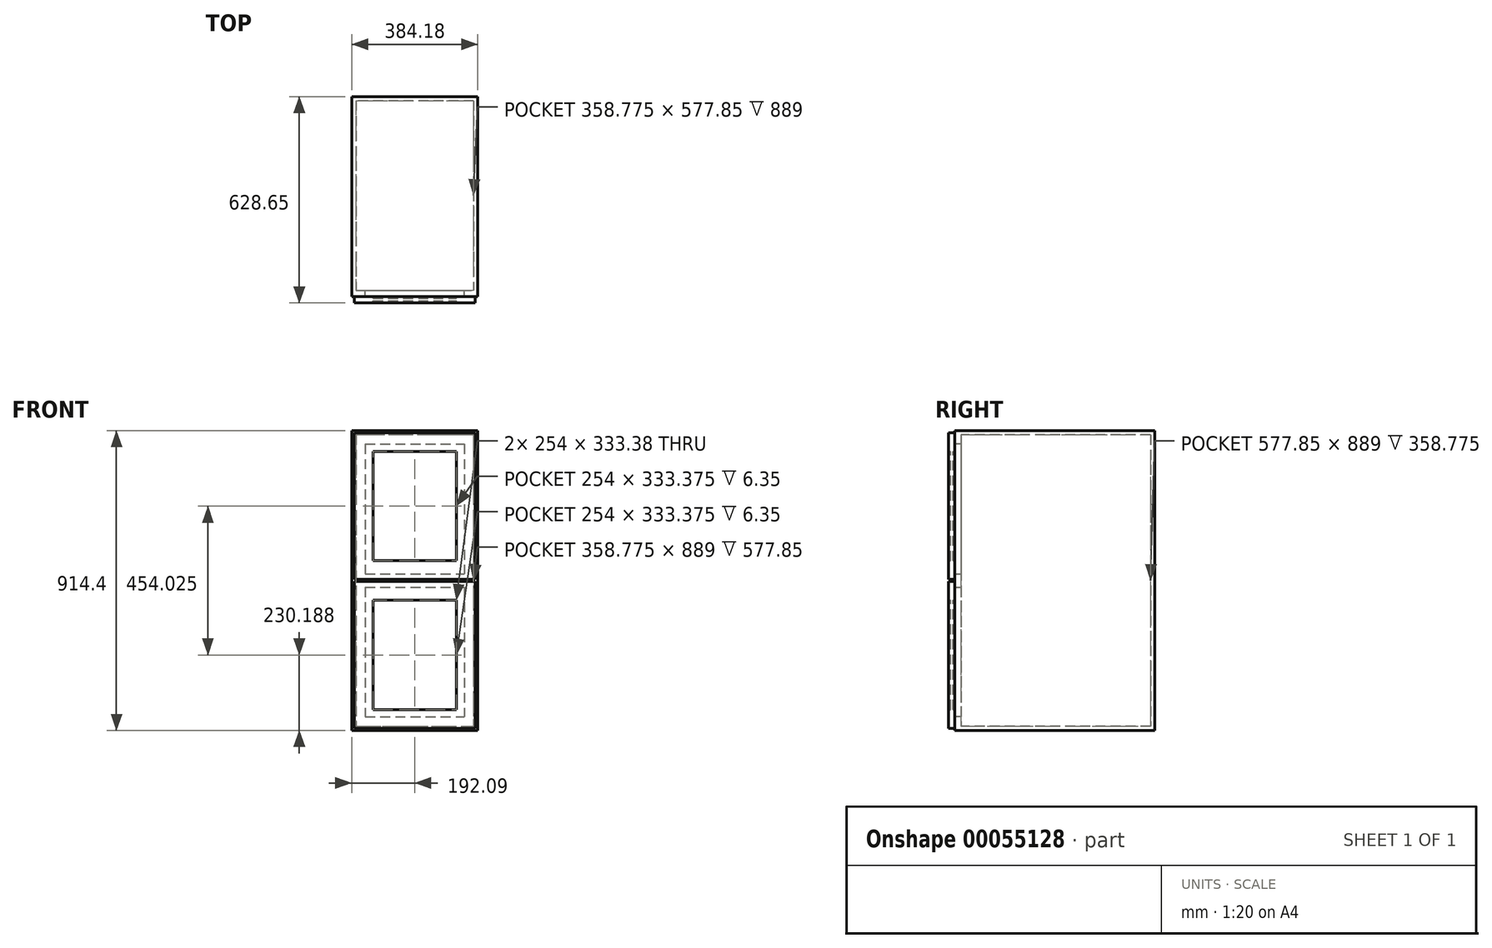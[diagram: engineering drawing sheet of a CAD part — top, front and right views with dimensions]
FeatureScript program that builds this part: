
annotation { "Feature Type Name" : "Feature", "Feature Type Description" : "" }
export const myFeature = defineFeature(function(context is Context, id is Id, definition is map)
    precondition{}
    {
        {
            var Q0;
            Q0=qCreatedBy(makeId("Top.planeOp"),FACE);
            var sketch = newSketch(context, id + "F0", { "sketchPlane" : qUnion([Q0])});
            skLineSegment(sketch, "E0.rect.bottom", {"start": v(192.09, 304.8) * mm, "end": v(-192.09, 304.8) * mm});
            skLineSegment(sketch, "E0.rect.top", {"start": v(192.09, -304.8) * mm, "end": v(-192.09, -304.8) * mm});
            skLineSegment(sketch, "E0.rect.left", {"start": v(192.09, 304.8) * mm, "end": v(192.09, -304.8) * mm});
            skLineSegment(sketch, "E0.rect.right", {"start": v(-192.09, 304.8) * mm, "end": v(-192.09, -304.8) * mm});
            skPoint(sketch, "E0.rect.middle", {"position": v(0, 0) * mm});
            skSolve(sketch);
        }
        {
            var Q0;
            Q0=qSketchRegion(id+"F0",true);
            extrude(context, id + "F1", {"entities" : qUnion([Q0]), "depth" : 914.4 * mm});
        }
        {
            var Q0;
            Q0=makeQuery(id+"F1.opExtrude","SWEPT_FACE",FACE,{"disambiguationData":[OSD([sQuery(id+"F0.wireOp",EDGE,"E0.rect.top")])]});
            shell(context, id + "F2", {"entities" : qUnion([Q0]), "thickness" : 12.7 * mm});
        }
        {
            var Q0;
            Q0=makeQuery(id+"F1.opExtrude","SWEPT_FACE",FACE,{"disambiguationData":[OSD([sQuery(id+"F0.wireOp",EDGE,"E0.rect.top")])]});
            var sketch = newSketch(context, id + "F3", { "sketchPlane" : qUnion([Q0])});
            skLineSegment(sketch, "E1", {"start": v(-192.09, 457.2) * mm, "end": v(192.09, 457.2) * mm, "construction": true});
            skLineSegment(sketch, "E2.rect.bottom", {"start": v(-192.09, 436.56) * mm, "end": v(192.09, 436.56) * mm});
            skLineSegment(sketch, "E2.rect.top", {"start": v(-192.09, 477.84) * mm, "end": v(192.09, 477.84) * mm});
            skLineSegment(sketch, "E2.rect.left", {"start": v(-192.09, 436.56) * mm, "end": v(-192.09, 477.84) * mm});
            skLineSegment(sketch, "E2.rect.right", {"start": v(192.09, 436.56) * mm, "end": v(192.09, 477.84) * mm});
            skPoint(sketch, "E2.rect.middle", {"position": v(0, 457.2) * mm});
            skLineSegment(sketch, "E3.bottom", {"start": v(-184.15, 6.35) * mm, "end": v(184.15, 6.35) * mm});
            skLineSegment(sketch, "E3.top", {"start": v(-184.15, 454.03) * mm, "end": v(184.15, 454.03) * mm});
            skLineSegment(sketch, "E3.left", {"start": v(-184.15, 6.35) * mm, "end": v(-184.15, 454.03) * mm});
            skLineSegment(sketch, "E3.right", {"start": v(184.15, 6.35) * mm, "end": v(184.15, 454.03) * mm});
            skLineSegment(sketch, "E4.rect.bottom", {"start": v(-150.81, 873.13) * mm, "end": v(150.81, 873.13) * mm});
            skLineSegment(sketch, "E4.rect.top", {"start": v(-150.81, 41.28) * mm, "end": v(150.81, 41.28) * mm});
            skLineSegment(sketch, "E4.rect.left", {"start": v(-150.81, 873.13) * mm, "end": v(-150.81, 41.28) * mm});
            skLineSegment(sketch, "E4.rect.right", {"start": v(150.81, 873.13) * mm, "end": v(150.81, 41.28) * mm});
            skLineSegment(sketch, "E5.bottom", {"start": v(-127, 63.5) * mm, "end": v(127, 63.5) * mm});
            skLineSegment(sketch, "E5.top", {"start": v(-127, 396.88) * mm, "end": v(127, 396.88) * mm});
            skLineSegment(sketch, "E5.left", {"start": v(-127, 63.5) * mm, "end": v(-127, 396.88) * mm});
            skLineSegment(sketch, "E5.right", {"start": v(127, 63.5) * mm, "end": v(127, 396.88) * mm});
            skLineSegment(sketch, "E6.bottom", {"start": v(-184.15, 460.38) * mm, "end": v(184.15, 460.38) * mm});
            skLineSegment(sketch, "E6.top", {"start": v(-184.15, 908.05) * mm, "end": v(184.15, 908.05) * mm});
            skLineSegment(sketch, "E6.left", {"start": v(-184.15, 460.38) * mm, "end": v(-184.15, 908.05) * mm});
            skLineSegment(sketch, "E6.right", {"start": v(184.15, 460.38) * mm, "end": v(184.15, 908.05) * mm});
            skLineSegment(sketch, "E7.bottom", {"start": v(-127, 517.53) * mm, "end": v(127, 517.53) * mm});
            skLineSegment(sketch, "E7.top", {"start": v(-127, 850.9) * mm, "end": v(127, 850.9) * mm});
            skLineSegment(sketch, "E7.left", {"start": v(-127, 517.53) * mm, "end": v(-127, 850.9) * mm});
            skLineSegment(sketch, "E7.right", {"start": v(127, 517.53) * mm, "end": v(127, 850.9) * mm});
            skSolve(sketch);
        }
        {
            var Q0;
            {var subQ9=sQuery(id+"F3.wireOp",EDGE,"E2.rect.left");Q0=makeQuery(id+"F3.imprint","IMPRINT",FACE,{"disambiguationData":[TD([[makeQuery(id+"F3.imprint","IMPRINT",EDGE,{"derivedFrom":subQ9}),1.0]])]});}
            var Q1;
            {var subQ0=sQuery(id+"F3.wireOp",EDGE,"E4.rect.left");var subQ1=sQuery(id+"F3.wireOp",EDGE,"E2.rect.bottom");var subQ2=makeQuery(id+"F3.imprint","INTERSECT",VERTEX,{"derivedFrom":[subQ1,subQ0]});Q1=makeQuery(id+"F3.imprint","IMPRINT",FACE,{"disambiguationData":[TD([[makeQuery(id+"F3.imprint","IMPRINT",EDGE,{"disambiguationData":[TD([[subQ2,1.0]])],"derivedFrom":subQ0}),-1.0]])]});}
            var Q2;
            {var subQ0=sQuery(id+"F3.wireOp",EDGE,"E4.rect.left");var subQ1=sQuery(id+"F3.wireOp",EDGE,"E2.rect.top");var subQ2=makeQuery(id+"F3.imprint","INTERSECT",VERTEX,{"derivedFrom":[subQ1,subQ0]});Q2=makeQuery(id+"F3.imprint","IMPRINT",FACE,{"disambiguationData":[TD([[makeQuery(id+"F3.imprint","IMPRINT",EDGE,{"disambiguationData":[TD([[subQ2,-1.0]])],"derivedFrom":subQ0}),-1.0]])]});}
            var Q3;
            {var subQ0=sQuery(id+"F3.wireOp",EDGE,"E4.rect.left");var subQ1=sQuery(id+"F3.wireOp",EDGE,"E2.rect.bottom");var subQ2=makeQuery(id+"F3.imprint","INTERSECT",VERTEX,{"derivedFrom":[subQ1,subQ0]});Q3=makeQuery(id+"F3.imprint","IMPRINT",FACE,{"disambiguationData":[TD([[makeQuery(id+"F3.imprint","IMPRINT",EDGE,{"disambiguationData":[TD([[subQ2,-1.0]])],"derivedFrom":subQ1}),1.0]])]});}
            var Q4;
            {var subQ0=sQuery(id+"F3.wireOp",EDGE,"E4.rect.left");var subQ1=sQuery(id+"F3.wireOp",EDGE,"E2.rect.top");var subQ2=makeQuery(id+"F3.imprint","INTERSECT",VERTEX,{"derivedFrom":[subQ1,subQ0]});Q4=makeQuery(id+"F3.imprint","IMPRINT",FACE,{"disambiguationData":[TD([[makeQuery(id+"F3.imprint","IMPRINT",EDGE,{"disambiguationData":[TD([[subQ2,-1.0]])],"derivedFrom":subQ1}),-1.0]])]});}
            var Q5;
            {var subQ0=sQuery(id+"F3.wireOp",EDGE,"E4.rect.right");var subQ1=sQuery(id+"F3.wireOp",EDGE,"E2.rect.bottom");var subQ2=makeQuery(id+"F3.imprint","INTERSECT",VERTEX,{"derivedFrom":[subQ1,subQ0]});Q5=makeQuery(id+"F3.imprint","IMPRINT",FACE,{"disambiguationData":[TD([[makeQuery(id+"F3.imprint","IMPRINT",EDGE,{"disambiguationData":[TD([[subQ2,1.0]])],"derivedFrom":subQ0}),1.0]])]});}
            var Q6;
            {var subQ0=sQuery(id+"F3.wireOp",EDGE,"E4.rect.right");var subQ1=sQuery(id+"F3.wireOp",EDGE,"E2.rect.top");var subQ2=makeQuery(id+"F3.imprint","INTERSECT",VERTEX,{"derivedFrom":[subQ1,subQ0]});Q6=makeQuery(id+"F3.imprint","IMPRINT",FACE,{"disambiguationData":[TD([[makeQuery(id+"F3.imprint","IMPRINT",EDGE,{"disambiguationData":[TD([[subQ2,-1.0]])],"derivedFrom":subQ0}),1.0]])]});}
            var Q7;
            {var subQ0=sQuery(id+"F3.wireOp",EDGE,"E2.rect.right");Q7=makeQuery(id+"F3.imprint","IMPRINT",FACE,{"disambiguationData":[TD([[makeQuery(id+"F3.imprint","IMPRINT",EDGE,{"derivedFrom":subQ0}),-1.0]])]});}
            var Q8;
            {var subQ0=sQuery(id+"F3.wireOp",EDGE,"E3.right");var subQ5=sQuery(id+"F3.wireOp",EDGE,"E3.top");var subQ6=makeQuery(id+"F3.imprint","INTERSECT",VERTEX,{"derivedFrom":[subQ5,subQ0]});Q8=makeQuery(id+"F3.imprint","IMPRINT",FACE,{"disambiguationData":[TD([[makeQuery(id+"F3.imprint","IMPRINT",EDGE,{"disambiguationData":[TD([[subQ6,1.0]])],"derivedFrom":subQ0}),1.0]])]});}
            var Q9;
            {var subQ0=sQuery(id+"F3.wireOp",EDGE,"E6.right");var subQ5=sQuery(id+"F3.wireOp",EDGE,"E6.bottom");var subQ6=makeQuery(id+"F3.imprint","INTERSECT",VERTEX,{"derivedFrom":[subQ5,subQ0]});Q9=makeQuery(id+"F3.imprint","IMPRINT",FACE,{"disambiguationData":[TD([[makeQuery(id+"F3.imprint","IMPRINT",EDGE,{"disambiguationData":[TD([[subQ6,-1.0]])],"derivedFrom":subQ0}),1.0]])]});}
            var Q10;
            {var subQ0=sQuery(id+"F3.wireOp",EDGE,"E4.rect.right");var subQ1=sQuery(id+"F3.wireOp",EDGE,"E3.top");var subQ2=makeQuery(id+"F3.imprint","INTERSECT",VERTEX,{"derivedFrom":[subQ1,subQ0]});Q10=makeQuery(id+"F3.imprint","IMPRINT",FACE,{"disambiguationData":[TD([[makeQuery(id+"F3.imprint","IMPRINT",EDGE,{"disambiguationData":[TD([[subQ2,1.0]])],"derivedFrom":subQ0}),1.0]])]});}
            var Q11;
            {var subQ0=sQuery(id+"F3.wireOp",EDGE,"E4.rect.left");var subQ1=sQuery(id+"F3.wireOp",EDGE,"E3.top");var subQ2=makeQuery(id+"F3.imprint","INTERSECT",VERTEX,{"derivedFrom":[subQ1,subQ0]});Q11=makeQuery(id+"F3.imprint","IMPRINT",FACE,{"disambiguationData":[TD([[makeQuery(id+"F3.imprint","IMPRINT",EDGE,{"disambiguationData":[TD([[subQ2,1.0]])],"derivedFrom":subQ0}),-1.0]])]});}
            var Q12;
            {var subQ0=sQuery(id+"F3.wireOp",EDGE,"E3.left");var subQ5=sQuery(id+"F3.wireOp",EDGE,"E3.top");var subQ6=makeQuery(id+"F3.imprint","INTERSECT",VERTEX,{"derivedFrom":[subQ5,subQ0]});Q12=makeQuery(id+"F3.imprint","IMPRINT",FACE,{"disambiguationData":[TD([[makeQuery(id+"F3.imprint","IMPRINT",EDGE,{"disambiguationData":[TD([[subQ6,1.0]])],"derivedFrom":subQ0}),-1.0]])]});}
            var Q13;
            {var subQ0=sQuery(id+"F3.wireOp",EDGE,"E6.left");var subQ5=sQuery(id+"F3.wireOp",EDGE,"E6.bottom");var subQ6=makeQuery(id+"F3.imprint","INTERSECT",VERTEX,{"derivedFrom":[subQ5,subQ0]});Q13=makeQuery(id+"F3.imprint","IMPRINT",FACE,{"disambiguationData":[TD([[makeQuery(id+"F3.imprint","IMPRINT",EDGE,{"disambiguationData":[TD([[subQ6,-1.0]])],"derivedFrom":subQ0}),-1.0]])]});}
            var Q14;
            {var subQ0=sQuery(id+"F3.wireOp",EDGE,"E4.rect.left");var subQ1=sQuery(id+"F3.wireOp",EDGE,"E3.top");var subQ2=makeQuery(id+"F3.imprint","INTERSECT",VERTEX,{"derivedFrom":[subQ1,subQ0]});Q14=makeQuery(id+"F3.imprint","IMPRINT",FACE,{"disambiguationData":[TD([[makeQuery(id+"F3.imprint","IMPRINT",EDGE,{"disambiguationData":[TD([[subQ2,-1.0]])],"derivedFrom":subQ1}),1.0]])]});}
            extrude(context, id + "F4", {"entities" : qUnion([Q0, Q1, Q2, Q3, Q4, Q5, Q6, Q7, Q8, Q9, Q10, Q11, Q12, Q13, Q14]), "operationType" : NewBodyOperationType.ADD, "oppositeDirection" : true, "depth" : 19.05 * mm});
        }
        {
            var Q0;
            {var subQ1=sQuery(id+"F3.wireOp",EDGE,"E4.rect.bottom");Q0=makeQuery(id+"F3.imprint","IMPRINT",FACE,{"disambiguationData":[TD([[makeQuery(id+"F3.imprint","IMPRINT",EDGE,{"derivedFrom":subQ1}),1.0]])]});}
            var Q1;
            {var subQ0=sQuery(id+"F0.wireOp",EDGE,"E0.rect.top");var subQ1=makeQuery(id+"F1.opExtrude","CAP_EDGE",EDGE,{"disambiguationData":[OSD([subQ0])],"isStart":false});Q1=makeQuery(id+"F3.imprint","IMPRINT",FACE,{"disambiguationData":[TD([[makeQuery(id+"F3.imprint","IMPRINT",EDGE,{"derivedFrom":subQ1}),1.0]])]});}
            var Q2;
            {var subQ0=sQuery(id+"F3.wireOp",EDGE,"E4.rect.top");Q2=makeQuery(id+"F3.imprint","IMPRINT",FACE,{"disambiguationData":[TD([[makeQuery(id+"F3.imprint","IMPRINT",EDGE,{"derivedFrom":subQ0}),-1.0]])]});}
            var Q3;
            {var subQ1=sQuery(id+"F3.wireOp",EDGE,"E3.bottom");Q3=makeQuery(id+"F3.imprint","IMPRINT",FACE,{"disambiguationData":[TD([[makeQuery(id+"F3.imprint","IMPRINT",EDGE,{"derivedFrom":subQ1}),-1.0]])]});}
            var Q4;
            {var subQ0=sQuery(id+"F3.wireOp",EDGE,"E3.bottom");Q4=makeQuery(id+"F3.imprint","IMPRINT",FACE,{"disambiguationData":[TD([[makeQuery(id+"F3.imprint","IMPRINT",EDGE,{"derivedFrom":subQ0}),1.0]])]});}
            var Q5;
            {var subQ0=sQuery(id+"F3.wireOp",EDGE,"E4.rect.left");var subQ1=sQuery(id+"F3.wireOp",EDGE,"E2.rect.bottom");var subQ2=makeQuery(id+"F3.imprint","INTERSECT",VERTEX,{"derivedFrom":[subQ1,subQ0]});Q5=makeQuery(id+"F3.imprint","IMPRINT",FACE,{"disambiguationData":[TD([[makeQuery(id+"F3.imprint","IMPRINT",EDGE,{"disambiguationData":[TD([[subQ2,1.0]])],"derivedFrom":subQ0}),-1.0]])]});}
            var Q6;
            {var subQ0=sQuery(id+"F3.wireOp",EDGE,"E2.rect.left");Q6=makeQuery(id+"F3.imprint","IMPRINT",FACE,{"disambiguationData":[TD([[makeQuery(id+"F3.imprint","IMPRINT",EDGE,{"derivedFrom":subQ0}),1.0]])]});}
            var Q7;
            {var subQ0=sQuery(id+"F3.wireOp",EDGE,"E3.left");var subQ5=sQuery(id+"F3.wireOp",EDGE,"E3.top");var subQ6=makeQuery(id+"F3.imprint","INTERSECT",VERTEX,{"derivedFrom":[subQ5,subQ0]});Q7=makeQuery(id+"F3.imprint","IMPRINT",FACE,{"disambiguationData":[TD([[makeQuery(id+"F3.imprint","IMPRINT",EDGE,{"disambiguationData":[TD([[subQ6,1.0]])],"derivedFrom":subQ0}),-1.0]])]});}
            var Q8;
            {var subQ0=sQuery(id+"F3.wireOp",EDGE,"E4.rect.left");var subQ1=sQuery(id+"F3.wireOp",EDGE,"E2.rect.top");var subQ2=makeQuery(id+"F3.imprint","INTERSECT",VERTEX,{"derivedFrom":[subQ1,subQ0]});Q8=makeQuery(id+"F3.imprint","IMPRINT",FACE,{"disambiguationData":[TD([[makeQuery(id+"F3.imprint","IMPRINT",EDGE,{"disambiguationData":[TD([[subQ2,-1.0]])],"derivedFrom":subQ0}),-1.0]])]});}
            var Q9;
            {var subQ0=sQuery(id+"F3.wireOp",EDGE,"E4.rect.right");var subQ1=sQuery(id+"F3.wireOp",EDGE,"E2.rect.top");var subQ2=makeQuery(id+"F3.imprint","INTERSECT",VERTEX,{"derivedFrom":[subQ1,subQ0]});Q9=makeQuery(id+"F3.imprint","IMPRINT",FACE,{"disambiguationData":[TD([[makeQuery(id+"F3.imprint","IMPRINT",EDGE,{"disambiguationData":[TD([[subQ2,-1.0]])],"derivedFrom":subQ0}),1.0]])]});}
            var Q10;
            {var subQ0=sQuery(id+"F3.wireOp",EDGE,"E4.rect.right");var subQ1=sQuery(id+"F3.wireOp",EDGE,"E2.rect.bottom");var subQ2=makeQuery(id+"F3.imprint","INTERSECT",VERTEX,{"derivedFrom":[subQ1,subQ0]});Q10=makeQuery(id+"F3.imprint","IMPRINT",FACE,{"disambiguationData":[TD([[makeQuery(id+"F3.imprint","IMPRINT",EDGE,{"disambiguationData":[TD([[subQ2,1.0]])],"derivedFrom":subQ0}),1.0]])]});}
            var Q11;
            {var subQ7=sQuery(id+"F3.wireOp",EDGE,"E2.rect.right");Q11=makeQuery(id+"F3.imprint","IMPRINT",FACE,{"disambiguationData":[TD([[makeQuery(id+"F3.imprint","IMPRINT",EDGE,{"derivedFrom":subQ7}),-1.0]])]});}
            var Q12;
            {var subQ0=sQuery(id+"F3.wireOp",EDGE,"E3.right");var subQ5=sQuery(id+"F3.wireOp",EDGE,"E3.top");var subQ6=makeQuery(id+"F3.imprint","INTERSECT",VERTEX,{"derivedFrom":[subQ5,subQ0]});Q12=makeQuery(id+"F3.imprint","IMPRINT",FACE,{"disambiguationData":[TD([[makeQuery(id+"F3.imprint","IMPRINT",EDGE,{"disambiguationData":[TD([[subQ6,1.0]])],"derivedFrom":subQ0}),1.0]])]});}
            extrude(context, id + "F5", {"entities" : qUnion([Q0, Q1, Q2, Q3, Q4, Q5, Q6, Q7, Q8, Q9, Q10, Q11, Q12]), "operationType" : NewBodyOperationType.ADD, "oppositeDirection" : true, "depth" : 19.05 * mm});
        }
        {
            var Q0;
            {var subQ0=sQuery(id+"F3.wireOp",EDGE,"E4.rect.top");Q0=makeQuery(id+"F3.imprint","IMPRINT",FACE,{"disambiguationData":[TD([[makeQuery(id+"F3.imprint","IMPRINT",EDGE,{"derivedFrom":subQ0}),-1.0]])]});}
            var Q1;
            {var subQ0=sQuery(id+"F3.wireOp",EDGE,"E3.bottom");Q1=makeQuery(id+"F3.imprint","IMPRINT",FACE,{"disambiguationData":[TD([[makeQuery(id+"F3.imprint","IMPRINT",EDGE,{"derivedFrom":subQ0}),1.0]])]});}
            var Q2;
            {var subQ1=sQuery(id+"F3.wireOp",EDGE,"E4.rect.top");Q2=makeQuery(id+"F3.imprint","IMPRINT",FACE,{"disambiguationData":[TD([[makeQuery(id+"F3.imprint","IMPRINT",EDGE,{"derivedFrom":subQ1}),1.0]])]});}
            var Q3;
            {var subQ0=sQuery(id+"F3.wireOp",EDGE,"E4.rect.left");var subQ1=sQuery(id+"F3.wireOp",EDGE,"E2.rect.bottom");var subQ2=makeQuery(id+"F3.imprint","INTERSECT",VERTEX,{"derivedFrom":[subQ1,subQ0]});Q3=makeQuery(id+"F3.imprint","IMPRINT",FACE,{"disambiguationData":[TD([[makeQuery(id+"F3.imprint","IMPRINT",EDGE,{"disambiguationData":[TD([[subQ2,-1.0]])],"derivedFrom":subQ1}),1.0]])]});}
            var Q4;
            {var subQ0=sQuery(id+"F3.wireOp",EDGE,"E4.rect.left");var subQ1=sQuery(id+"F3.wireOp",EDGE,"E2.rect.bottom");var subQ2=makeQuery(id+"F3.imprint","INTERSECT",VERTEX,{"derivedFrom":[subQ1,subQ0]});Q4=makeQuery(id+"F3.imprint","IMPRINT",FACE,{"disambiguationData":[TD([[makeQuery(id+"F3.imprint","IMPRINT",EDGE,{"disambiguationData":[TD([[subQ2,1.0]])],"derivedFrom":subQ0}),-1.0]])]});}
            var Q5;
            {var subQ0=sQuery(id+"F3.wireOp",EDGE,"E4.rect.right");var subQ1=sQuery(id+"F3.wireOp",EDGE,"E2.rect.bottom");var subQ2=makeQuery(id+"F3.imprint","INTERSECT",VERTEX,{"derivedFrom":[subQ1,subQ0]});Q5=makeQuery(id+"F3.imprint","IMPRINT",FACE,{"disambiguationData":[TD([[makeQuery(id+"F3.imprint","IMPRINT",EDGE,{"disambiguationData":[TD([[subQ2,1.0]])],"derivedFrom":subQ0}),1.0]])]});}
            var Q6;
            {var subQ0=sQuery(id+"F3.wireOp",EDGE,"E3.right");var subQ5=sQuery(id+"F3.wireOp",EDGE,"E3.top");var subQ6=makeQuery(id+"F3.imprint","INTERSECT",VERTEX,{"derivedFrom":[subQ5,subQ0]});Q6=makeQuery(id+"F3.imprint","IMPRINT",FACE,{"disambiguationData":[TD([[makeQuery(id+"F3.imprint","IMPRINT",EDGE,{"disambiguationData":[TD([[subQ6,1.0]])],"derivedFrom":subQ0}),1.0]])]});}
            var Q7;
            {var subQ0=sQuery(id+"F3.wireOp",EDGE,"E3.left");var subQ5=sQuery(id+"F3.wireOp",EDGE,"E3.top");var subQ6=makeQuery(id+"F3.imprint","INTERSECT",VERTEX,{"derivedFrom":[subQ5,subQ0]});Q7=makeQuery(id+"F3.imprint","IMPRINT",FACE,{"disambiguationData":[TD([[makeQuery(id+"F3.imprint","IMPRINT",EDGE,{"disambiguationData":[TD([[subQ6,1.0]])],"derivedFrom":subQ0}),-1.0]])]});}
            var Q8;
            {var subQ0=sQuery(id+"F3.wireOp",EDGE,"E4.rect.bottom");Q8=makeQuery(id+"F3.imprint","IMPRINT",FACE,{"disambiguationData":[TD([[makeQuery(id+"F3.imprint","IMPRINT",EDGE,{"derivedFrom":subQ0}),1.0]])]});}
            var Q9;
            {var subQ1=sQuery(id+"F3.wireOp",EDGE,"E4.rect.bottom");Q9=makeQuery(id+"F3.imprint","IMPRINT",FACE,{"disambiguationData":[TD([[makeQuery(id+"F3.imprint","IMPRINT",EDGE,{"derivedFrom":subQ1}),-1.0]])]});}
            var Q10;
            {var subQ0=sQuery(id+"F3.wireOp",EDGE,"E4.rect.left");var subQ1=sQuery(id+"F3.wireOp",EDGE,"E2.rect.top");var subQ2=makeQuery(id+"F3.imprint","INTERSECT",VERTEX,{"derivedFrom":[subQ1,subQ0]});Q10=makeQuery(id+"F3.imprint","IMPRINT",FACE,{"disambiguationData":[TD([[makeQuery(id+"F3.imprint","IMPRINT",EDGE,{"disambiguationData":[TD([[subQ2,-1.0]])],"derivedFrom":subQ0}),-1.0]])]});}
            var Q11;
            {var subQ0=sQuery(id+"F3.wireOp",EDGE,"E4.rect.left");var subQ1=sQuery(id+"F3.wireOp",EDGE,"E2.rect.top");var subQ2=makeQuery(id+"F3.imprint","INTERSECT",VERTEX,{"derivedFrom":[subQ1,subQ0]});Q11=makeQuery(id+"F3.imprint","IMPRINT",FACE,{"disambiguationData":[TD([[makeQuery(id+"F3.imprint","IMPRINT",EDGE,{"disambiguationData":[TD([[subQ2,-1.0]])],"derivedFrom":subQ1}),-1.0]])]});}
            var Q12;
            {var subQ0=sQuery(id+"F3.wireOp",EDGE,"E4.rect.right");var subQ1=sQuery(id+"F3.wireOp",EDGE,"E2.rect.top");var subQ2=makeQuery(id+"F3.imprint","INTERSECT",VERTEX,{"derivedFrom":[subQ1,subQ0]});Q12=makeQuery(id+"F3.imprint","IMPRINT",FACE,{"disambiguationData":[TD([[makeQuery(id+"F3.imprint","IMPRINT",EDGE,{"disambiguationData":[TD([[subQ2,-1.0]])],"derivedFrom":subQ0}),1.0]])]});}
            var Q13;
            {var subQ0=sQuery(id+"F3.wireOp",EDGE,"E6.right");var subQ5=sQuery(id+"F3.wireOp",EDGE,"E6.bottom");var subQ6=makeQuery(id+"F3.imprint","INTERSECT",VERTEX,{"derivedFrom":[subQ5,subQ0]});Q13=makeQuery(id+"F3.imprint","IMPRINT",FACE,{"disambiguationData":[TD([[makeQuery(id+"F3.imprint","IMPRINT",EDGE,{"disambiguationData":[TD([[subQ6,-1.0]])],"derivedFrom":subQ0}),1.0]])]});}
            var Q14;
            {var subQ1=sQuery(id+"F3.wireOp",EDGE,"E6.top");Q14=makeQuery(id+"F3.imprint","IMPRINT",FACE,{"disambiguationData":[TD([[makeQuery(id+"F3.imprint","IMPRINT",EDGE,{"derivedFrom":subQ1}),-1.0]])]});}
            var Q15;
            {var subQ0=sQuery(id+"F3.wireOp",EDGE,"E6.left");var subQ5=sQuery(id+"F3.wireOp",EDGE,"E6.bottom");var subQ6=makeQuery(id+"F3.imprint","INTERSECT",VERTEX,{"derivedFrom":[subQ5,subQ0]});Q15=makeQuery(id+"F3.imprint","IMPRINT",FACE,{"disambiguationData":[TD([[makeQuery(id+"F3.imprint","IMPRINT",EDGE,{"disambiguationData":[TD([[subQ6,-1.0]])],"derivedFrom":subQ0}),-1.0]])]});}
            extrude(context, id + "F6", {"entities" : qUnion([Q0, Q1, Q2, Q3, Q4, Q5, Q6, Q7, Q8, Q9, Q10, Q11, Q12, Q13, Q14, Q15]), "operationType" : NewBodyOperationType.ADD, "depth" : 19.05 * mm});
        }
        {
            var Q0;
            Q0=makeQuery(id+"F6.opExtrude","SWEPT_FACE",FACE,{"disambiguationData":[OSD([sQuery(id+"F3.wireOp",EDGE,"E5.right")])]});
            var sketch = newSketch(context, id + "F7", { "sketchPlane" : qUnion([Q0])});
            skLineSegment(sketch, "E8.bottom", {"start": v(309.56, 63.5) * mm, "end": v(317.5, 63.5) * mm});
            skLineSegment(sketch, "E8.top", {"start": v(309.56, 396.88) * mm, "end": v(317.5, 396.88) * mm});
            skLineSegment(sketch, "E8.left", {"start": v(309.56, 63.5) * mm, "end": v(309.56, 396.88) * mm});
            skLineSegment(sketch, "E8.right", {"start": v(317.5, 63.5) * mm, "end": v(317.5, 396.88) * mm});
            skLineSegment(sketch, "E9.bottom", {"start": v(309.56, 517.53) * mm, "end": v(317.5, 517.53) * mm});
            skLineSegment(sketch, "E9.top", {"start": v(309.56, 850.9) * mm, "end": v(317.5, 850.9) * mm});
            skLineSegment(sketch, "E9.left", {"start": v(309.56, 517.53) * mm, "end": v(309.56, 850.9) * mm});
            skLineSegment(sketch, "E9.right", {"start": v(317.5, 517.53) * mm, "end": v(317.5, 850.9) * mm});
            skSolve(sketch);
        }
        {
            var Q0;
            Q0=qSketchRegion(id+"F7",true);
            extrude(context, id + "F8", {"entities" : qUnion([Q0]), "operationType" : NewBodyOperationType.ADD, "endBound" : BoundingType.UP_TO_NEXT, "depth" : 25.4 * mm});
        }
    });
